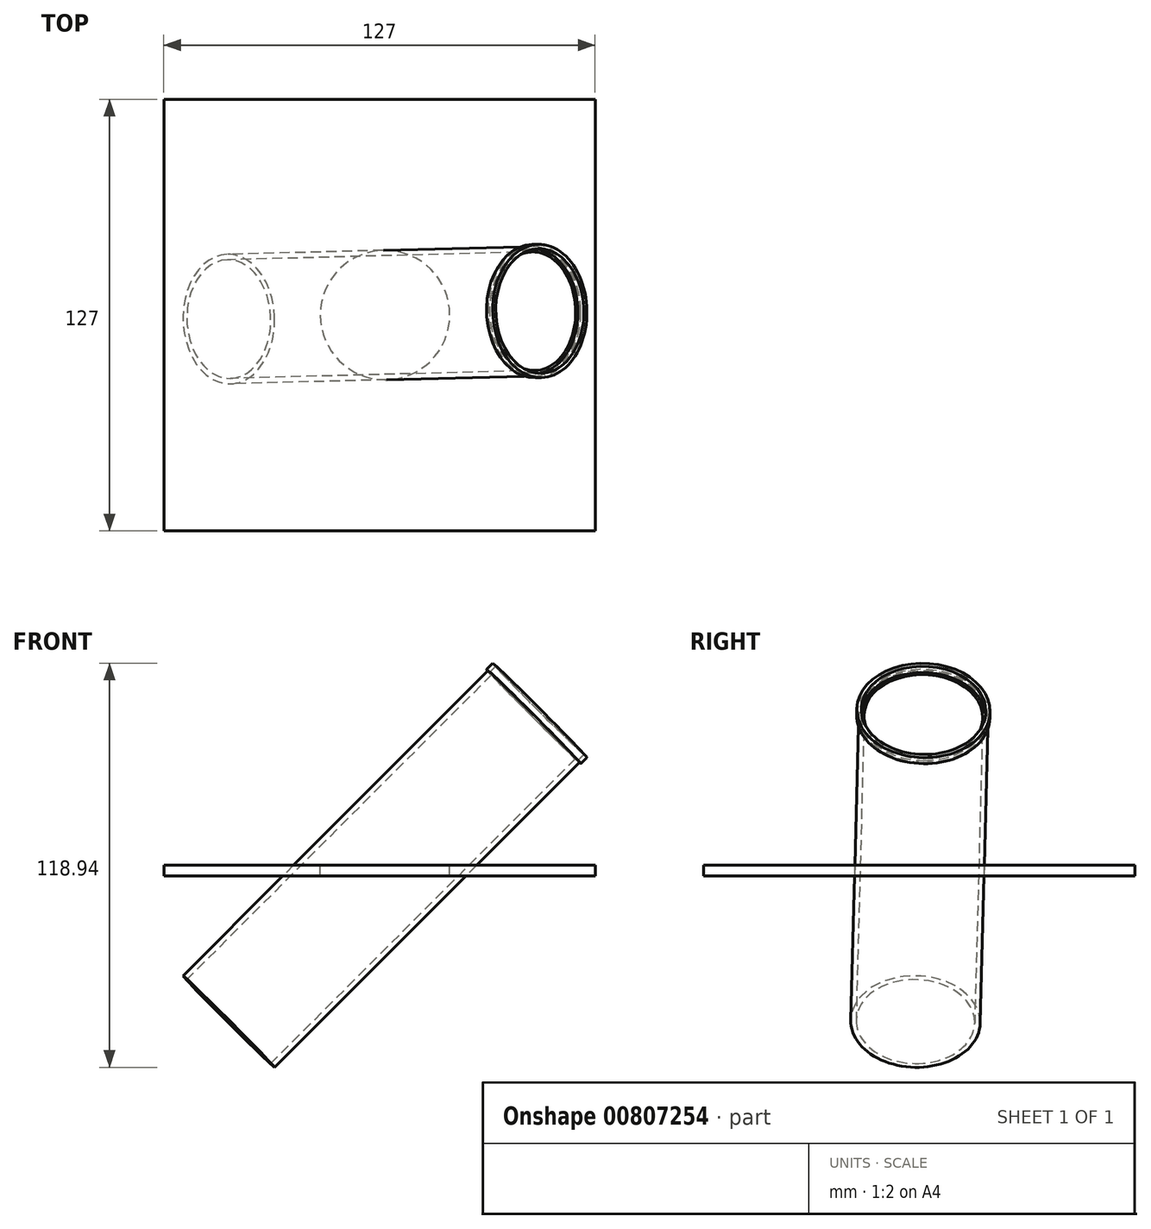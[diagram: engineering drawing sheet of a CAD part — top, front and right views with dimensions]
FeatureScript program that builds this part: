
annotation { "Feature Type Name" : "Feature", "Feature Type Description" : "" }
export const myFeature = defineFeature(function(context is Context, id is Id, definition is map)
    precondition{}
    {
        {
            var Q0;
            Q0=qCreatedBy(makeId("Top.planeOp"),FACE);
            var sketch = newSketch(context, id + "F0", { "sketchPlane" : qUnion([Q0])});
            skCircle(sketch, "E0", {"center": v(0, 0) * mm, "radius": 19.05 * mm});
            skCircle(sketch, "E1", {"center": v(0, 0) * mm, "radius": 17.46 * mm});
            skLineSegment(sketch, "E2", {"start": v(0, 0) * mm, "end": v(-1.65, 63.48) * mm, "construction": true});
            skLineSegment(sketch, "E3", {"start": v(-1.65, 63.48) * mm, "end": v(61.85, 63.48) * mm});
            skLineSegment(sketch, "E4", {"start": v(61.85, 63.48) * mm, "end": v(61.85, -63.52) * mm});
            skLineSegment(sketch, "E5", {"start": v(61.85, -63.52) * mm, "end": v(-65.15, -63.52) * mm});
            skLineSegment(sketch, "E6", {"start": v(-65.15, -63.52) * mm, "end": v(-65.15, 63.48) * mm});
            skLineSegment(sketch, "E7", {"start": v(-65.15, 63.48) * mm, "end": v(-1.65, 63.48) * mm});
            skLineSegment(sketch, "E8", {"start": v(0, 0) * mm, "end": v(50.74, 0) * mm, "construction": true});
            skSolve(sketch);
        }
        {
            var Q0;
            Q0=makeQuery(id+"F0.imprint","IMPRINT",FACE,{"disambiguationData":[TD([[makeQuery(id+"F0.imprint","IMPRINT",EDGE,{"derivedFrom":sQuery(id+"F0.wireOp",EDGE,"E0")}),1.0]])]});
            extrude(context, id + "F1", {"entities" : qUnion([Q0]), "depth" : 127 * mm, "offsetDistance" : 25.4 * mm});
        }
        {
            var Q0;
            Q0=makeQuery(id+"F0.imprint","IMPRINT",FACE,{"disambiguationData":[TD([[makeQuery(id+"F0.imprint","IMPRINT",EDGE,{"derivedFrom":sQuery(id+"F0.wireOp",EDGE,"E0")}),-1.0]])]});
            extrude(context, id + "F2", {"entities" : qUnion([Q0]), "oppositeDirection" : true, "depth" : 3.17 * mm, "offsetDistance" : 25.4 * mm});
        }
        {
            var Q0;
            Q0=makeQuery(id+"F1.opExtrude","SWEPT_BODY",BODY,{"disambiguationData":[OSD([sQuery(id+"F0.wireOp",EDGE,"E0"),sQuery(id+"F0.wireOp",EDGE,"E1")])]});
            transform(context, id + "F3", {"entities" : qUnion([Q0]), "transformType" : TransformType.TRANSLATION_3D, "dx" : 0 * mm, "dy" : 0 * mm, "dz" : -65.1 * mm, "makeCopy" : false});
        }
        {
            var Q0;
            Q0=makeQuery(id+"F1.opExtrude","SWEPT_BODY",BODY,{"disambiguationData":[OSD([sQuery(id+"F0.wireOp",EDGE,"E0"),sQuery(id+"F0.wireOp",EDGE,"E1")])]});
            var Q1;
            Q1=sQuery(id+"F0.wireOp",EDGE,"E2");
            transform(context, id + "F4", {"entities" : qUnion([Q0]), "transformType" : TransformType.ROTATION, "transformAxis" : qUnion([Q1]), "angle" : 45 * degree, "makeCopy" : false});
        }
        {
            var Q0;
            Q0=makeQuery(id+"F1.opExtrude","CAP_FACE",FACE,{"disambiguationData":[OSD([sQuery(id+"F0.wireOp",EDGE,"E0"),sQuery(id+"F0.wireOp",EDGE,"E1")])],"isStart":false});
            var sketch = newSketch(context, id + "F5", { "sketchPlane" : qUnion([Q0])});
            skCircle(sketch, "E9", {"center": v(0, 0) * mm, "radius": 19.62 * mm});
            skCircle(sketch, "E10", {"center": v(0, 0) * mm, "radius": 18.35 * mm});
            skSolve(sketch);
        }
        {
            var Q0;
            Q0=makeQuery(id+"F5.imprint","IMPRINT",FACE,{"disambiguationData":[TD([[makeQuery(id+"F5.imprint","IMPRINT",EDGE,{"derivedFrom":sQuery(id+"F5.wireOp",EDGE,"E9")}),1.0]])]});
            var Q1;
            Q1=makeQuery(id+"F5.imprint","IMPRINT",FACE,{"disambiguationData":[TD([[makeQuery(id+"F5.imprint","IMPRINT",EDGE,{"derivedFrom":sQuery(id+"F5.wireOp",EDGE,"E10")}),-1.0]])]});
            extrude(context, id + "F6", {"entities" : qUnion([Q0, Q1]), "operationType" : NewBodyOperationType.ADD, "depth" : 2.54 * mm, "offsetDistance" : 25.4 * mm});
        }
    });
